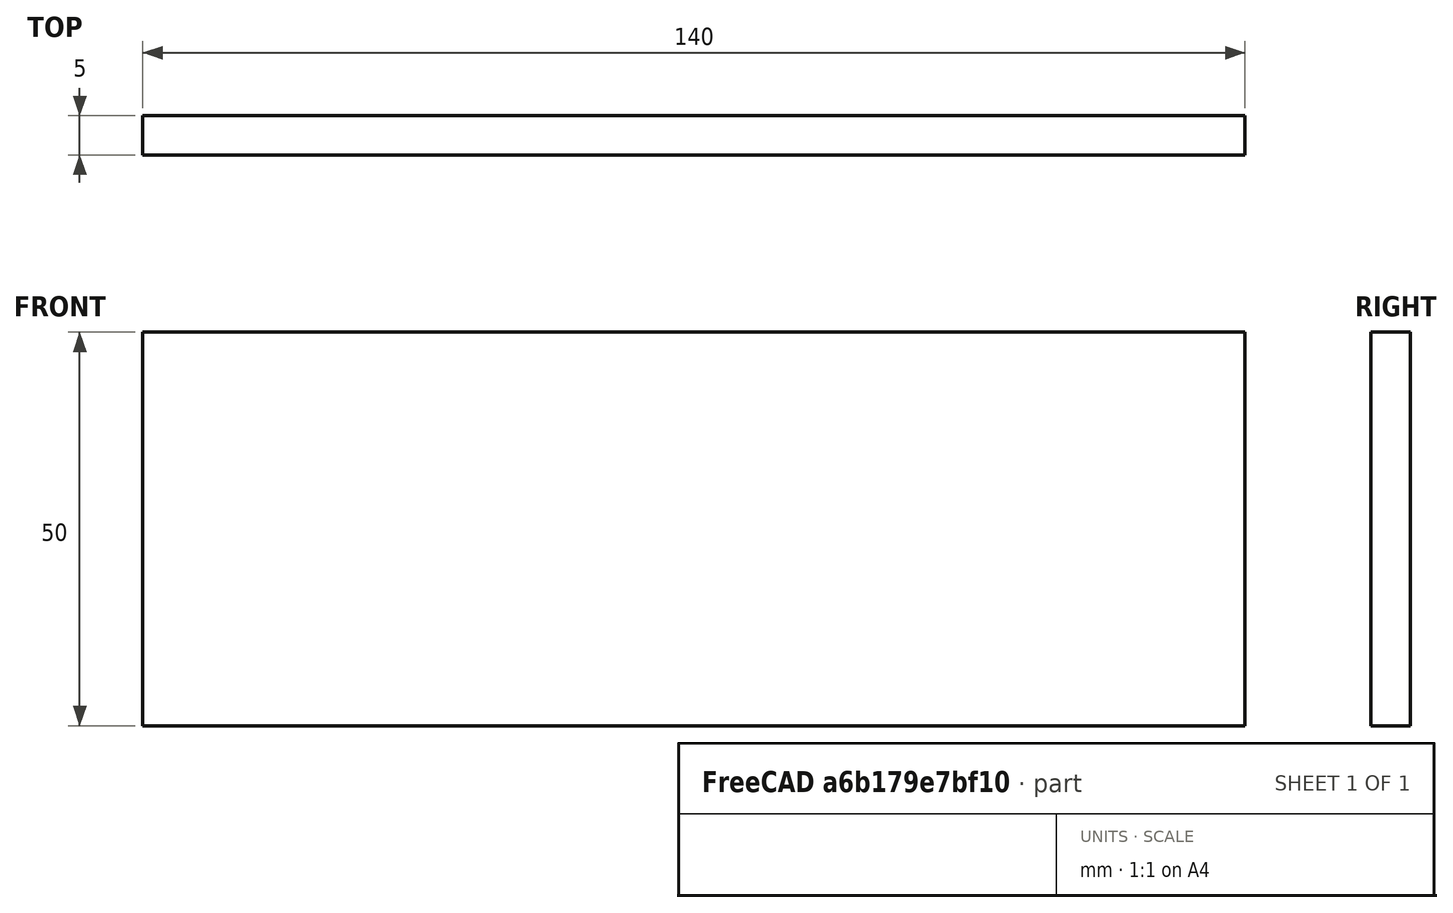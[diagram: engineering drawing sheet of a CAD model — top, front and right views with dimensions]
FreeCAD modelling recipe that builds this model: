
FCSTD DOCUMENT  (FreeCAD 0.15R4671 (Git))
Label: Flat Bar 140x5 EN10058 S235JR
License: All rights reserved
LicenseURL: http://en.wikipedia.org/wiki/All_rights_reserved
objects: Sketcher::SketchObject×1, Part::Extrusion×1
note: 2 computed .brp shape members not serialized (recipe doc carries the construction recipe); baked Part::Feature solids carry a one-line shape summary decoded from their .brp

FEATURE [Sketcher::SketchObject] Sketch
  sketch-geometry (4):
    g0: LineSegment StartX=-70 StartY=-2.5 StartZ=0 EndX=70 EndY=-2.5 EndZ=0
    g1: LineSegment StartX=70 StartY=-2.5 StartZ=0 EndX=70 EndY=2.5 EndZ=0
    g2: LineSegment StartX=70 StartY=2.5 StartZ=0 EndX=-70 EndY=2.5 EndZ=0
    g3: LineSegment StartX=-70 StartY=2.5 StartZ=0 EndX=-70 EndY=-2.5 EndZ=0
  constraints (12):
    c: Coincident(g0,g1)
    c: Coincident(g1,g2)
    c: Coincident(g2,g3)
    c: Coincident(g3,g0)
    c: Horizontal(g0)
    c: Horizontal(g2)
    c: Vertical(g1)
    c: Vertical(g3)
    c: Symmetric(g1,g2,g-2)
    c: Symmetric(g0,g1,g-1)
    c: DistanceY(g1) = 5
    c: DistanceX(g0) = 140
FEATURE [Part::Extrusion] Extrude  label="Flat Bar 140x5 EN10058 S235JR"
  Base = -> Sketch
  Dir = (0,0,50)
  Solid = true
